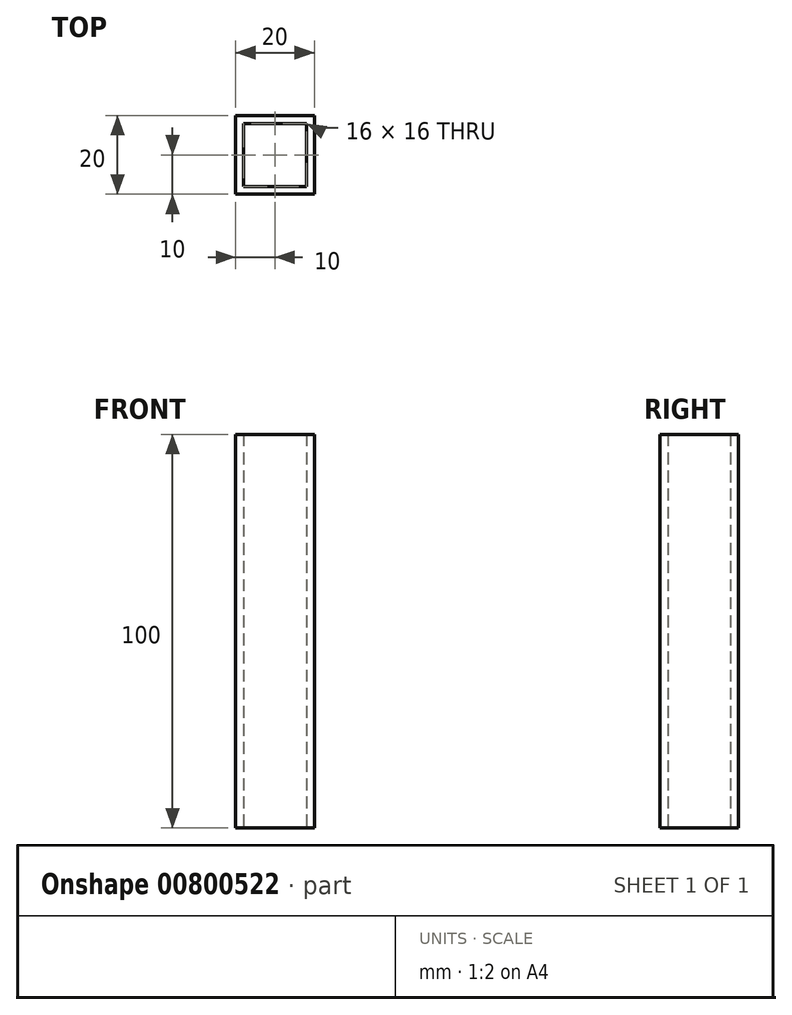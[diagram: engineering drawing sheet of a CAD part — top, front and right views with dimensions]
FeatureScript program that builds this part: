
annotation { "Feature Type Name" : "Feature", "Feature Type Description" : "" }
export const myFeature = defineFeature(function(context is Context, id is Id, definition is map)
    precondition{}
    {
        {
            var Q0;
            Q0=qCreatedBy(makeId("Top.planeOp"),FACE);
            var sketch = newSketch(context, id + "F0", { "sketchPlane" : qUnion([Q0])});
            skLineSegment(sketch, "E0.bottom", {"start": v(10, 10) * mm, "end": v(-10, 10) * mm});
            skLineSegment(sketch, "E0.top", {"start": v(10, -10) * mm, "end": v(-10, -10) * mm});
            skLineSegment(sketch, "E0.left", {"start": v(10, 10) * mm, "end": v(10, -10) * mm});
            skLineSegment(sketch, "E0.right", {"start": v(-10, 10) * mm, "end": v(-10, -10) * mm});
            skPoint(sketch, "E0.middle", {"position": v(0, 0) * mm});
            skLineSegment(sketch, "E1.0", {"start": v(-8, 8) * mm, "end": v(-8, -8) * mm});
            skLineSegment(sketch, "E1.1", {"start": v(8, 8) * mm, "end": v(-8, 8) * mm});
            skLineSegment(sketch, "E1.2", {"start": v(8, 8) * mm, "end": v(8, -8) * mm});
            skLineSegment(sketch, "E1.3", {"start": v(8, -8) * mm, "end": v(-8, -8) * mm});
            skSolve(sketch);
        }
        {
            var Q0;
            Q0=makeQuery(id+"F0.imprint","IMPRINT",FACE,{"disambiguationData":[TD([[makeQuery(id+"F0.imprint","IMPRINT",EDGE,{"derivedFrom":sQuery(id+"F0.wireOp",EDGE,"E0.bottom")}),1.0]])]});
            extrude(context, id + "F1", {"entities" : qUnion([Q0]), "depth" : 100 * mm, "offsetDistance" : 25 * mm});
        }
    });
